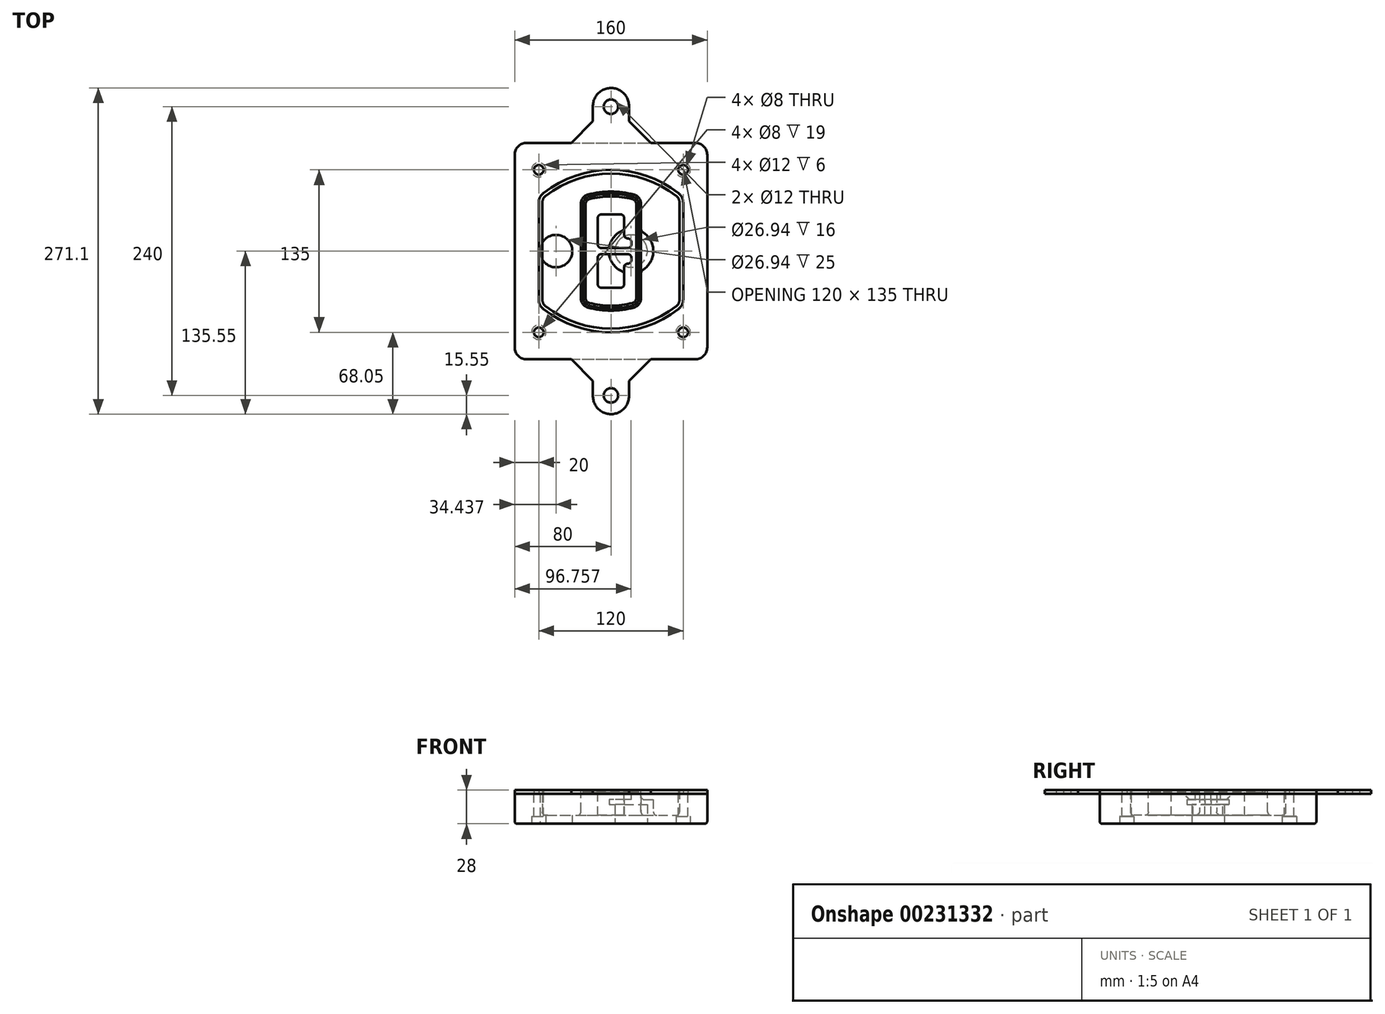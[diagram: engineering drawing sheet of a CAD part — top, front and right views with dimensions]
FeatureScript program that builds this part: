
annotation { "Feature Type Name" : "Feature", "Feature Type Description" : "" }
export const myFeature = defineFeature(function(context is Context, id is Id, definition is map)
    precondition{}
    {
        {
            var Q0;
            Q0=qCreatedBy(makeId("Top.planeOp"),FACE);
            var sketch = newSketch(context, id + "F0", { "sketchPlane" : qUnion([Q0])});
            skPoint(sketch, "E0.rect.middle", {"position": v(0, 0) * mm});
            skLineSegment(sketch, "E1.bottom", {"start": v(-70, -90) * mm, "end": v(70, -90) * mm});
            skLineSegment(sketch, "E1.top", {"start": v(-70, 90) * mm, "end": v(70, 90) * mm});
            skLineSegment(sketch, "E1.left", {"start": v(-80, -80) * mm, "end": v(-80, 80) * mm});
            skLineSegment(sketch, "E1.right", {"start": v(80, -80) * mm, "end": v(80, 80) * mm});
            skLineSegment(sketch, "E2", {"start": v(-80, 90) * mm, "end": v(80, -90) * mm, "construction": true});
            skLineSegment(sketch, "E3", {"start": v(80, 90) * mm, "end": v(-80, -90) * mm, "construction": true});
            skCircle(sketch, "E4", {"center": v(-60, 67.5) * mm, "radius": 4 * mm});
            skCircle(sketch, "E5", {"center": v(60, 67.5) * mm, "radius": 4 * mm});
            skCircle(sketch, "E6", {"center": v(60, -67.5) * mm, "radius": 4 * mm});
            skCircle(sketch, "E7", {"center": v(-60, -67.5) * mm, "radius": 4 * mm});
            skLineSegment(sketch, "E8", {"start": v(-60, 67.5) * mm, "end": v(60, 67.5) * mm, "construction": true});
            skLineSegment(sketch, "E9", {"start": v(60, 67.5) * mm, "end": v(60, -67.5) * mm, "construction": true});
            skLineSegment(sketch, "E10", {"start": v(60, -67.5) * mm, "end": v(-60, -67.5) * mm, "construction": true});
            skLineSegment(sketch, "E11", {"start": v(-60, -67.5) * mm, "end": v(-60, 67.5) * mm, "construction": true});
            skLineSegment(sketch, "E12", {"start": v(-60, 40.3) * mm, "end": v(-60, -40.3) * mm});
            skLineSegment(sketch, "E13", {"start": v(60, 40.3) * mm, "end": v(60, -40.3) * mm});
            skArc(sketch, "E14", {"start": v(56.15, 48.18) * mm, "mid": v(0, 67.5) * mm, "end": v(-56.15, 48.18) * mm});
            skArc(sketch, "E15", {"start": v(-56.15, -48.18) * mm, "mid": v(0, -67.5) * mm, "end": v(56.15, -48.18) * mm});
            skLineSegment(sketch, "E16", {"start": v(-60, 0) * mm, "end": v(60, 0) * mm, "construction": true});
            skPoint(sketch, "E17.visualSharp", {"position": v(-60, -45) * mm});
            skArc(sketch, "E17.filletArc", {"start": v(-60, -40.3) * mm, "mid": v(-58.99, -44.68) * mm, "end": v(-56.15, -48.18) * mm});
            skPoint(sketch, "E18.visualSharp", {"position": v(-60, 45) * mm});
            skArc(sketch, "E18.filletArc", {"start": v(-56.15, 48.18) * mm, "mid": v(-58.99, 44.68) * mm, "end": v(-60, 40.3) * mm});
            skPoint(sketch, "E19.visualSharp", {"position": v(60, 45) * mm});
            skArc(sketch, "E19.filletArc", {"start": v(60, 40.3) * mm, "mid": v(58.99, 44.68) * mm, "end": v(56.15, 48.18) * mm});
            skPoint(sketch, "E20.visualSharp", {"position": v(60, -45) * mm});
            skArc(sketch, "E20.filletArc", {"start": v(56.15, -48.18) * mm, "mid": v(58.99, -44.68) * mm, "end": v(60, -40.3) * mm});
            skPoint(sketch, "E21.visualSharp", {"position": v(-80, 90) * mm});
            skArc(sketch, "E21.filletArc", {"start": v(-70, 90) * mm, "mid": v(-77.07, 87.07) * mm, "end": v(-80, 80) * mm});
            skPoint(sketch, "E22.visualSharp", {"position": v(80, 90) * mm});
            skArc(sketch, "E22.filletArc", {"start": v(80, 80) * mm, "mid": v(77.07, 87.07) * mm, "end": v(70, 90) * mm});
            skPoint(sketch, "E23.visualSharp", {"position": v(80, -90) * mm});
            skArc(sketch, "E23.filletArc", {"start": v(70, -90) * mm, "mid": v(77.07, -87.07) * mm, "end": v(80, -80) * mm});
            skPoint(sketch, "E24.visualSharp", {"position": v(-80, -90) * mm});
            skArc(sketch, "E24.filletArc", {"start": v(-80, -80) * mm, "mid": v(-77.07, -87.07) * mm, "end": v(-70, -90) * mm});
            skArc(sketch, "E25.0", {"start": v(57, 40.3) * mm, "mid": v(56.3, 43.36) * mm, "end": v(54.3, 45.81) * mm});
            skLineSegment(sketch, "E25.1", {"start": v(57, 40.3) * mm, "end": v(57, -40.3) * mm});
            skArc(sketch, "E25.2", {"start": v(54.3, -45.81) * mm, "mid": v(56.3, -43.36) * mm, "end": v(57, -40.3) * mm});
            skArc(sketch, "E25.3", {"start": v(-54.3, -45.81) * mm, "mid": v(0, -64.5) * mm, "end": v(54.3, -45.81) * mm});
            skArc(sketch, "E25.4", {"start": v(-57, -40.3) * mm, "mid": v(-56.3, -43.36) * mm, "end": v(-54.3, -45.81) * mm});
            skArc(sketch, "E25.5", {"start": v(54.3, 45.81) * mm, "mid": v(0, 64.5) * mm, "end": v(-54.3, 45.81) * mm});
            skLineSegment(sketch, "E25.6", {"start": v(-57, 40.3) * mm, "end": v(-57, -40.3) * mm});
            skArc(sketch, "E25.7", {"start": v(-54.3, 45.81) * mm, "mid": v(-56.3, 43.36) * mm, "end": v(-57, 40.3) * mm});
            skArc(sketch, "E26.0", {"start": v(-58.62, 51.33) * mm, "mid": v(-62.58, 46.43) * mm, "end": v(-64, 40.3) * mm});
            skArc(sketch, "E26.1", {"start": v(58.62, 51.33) * mm, "mid": v(0, 71.5) * mm, "end": v(-58.62, 51.33) * mm});
            skArc(sketch, "E26.2", {"start": v(64, 40.3) * mm, "mid": v(62.58, 46.43) * mm, "end": v(58.62, 51.33) * mm});
            skLineSegment(sketch, "E26.3", {"start": v(64, 40.3) * mm, "end": v(64, -40.3) * mm});
            skArc(sketch, "E26.4", {"start": v(58.62, -51.33) * mm, "mid": v(62.58, -46.43) * mm, "end": v(64, -40.3) * mm});
            skLineSegment(sketch, "E26.5", {"start": v(-64, 40.3) * mm, "end": v(-64, -40.3) * mm});
            skArc(sketch, "E26.6", {"start": v(-58.62, -51.33) * mm, "mid": v(0, -71.5) * mm, "end": v(58.62, -51.33) * mm});
            skArc(sketch, "E26.7", {"start": v(-64, -40.3) * mm, "mid": v(-62.58, -46.43) * mm, "end": v(-58.62, -51.33) * mm});
            skSolve(sketch);
        }
        {
            var Q0;
            Q0=makeQuery(id+"F0.imprint","IMPRINT",FACE,{"disambiguationData":[TD([[makeQuery(id+"F0.imprint","IMPRINT",EDGE,{"derivedFrom":sQuery(id+"F0.wireOp",EDGE,"E1.bottom")}),1.0]])]});
            var Q1;
            Q1=makeQuery(id+"F0.imprint","IMPRINT",FACE,{"disambiguationData":[TD([[makeQuery(id+"F0.imprint","IMPRINT",EDGE,{"derivedFrom":sQuery(id+"F0.wireOp",EDGE,"E12")}),1.0]])]});
            var Q2;
            Q2=makeQuery(id+"F0.imprint","IMPRINT",FACE,{"disambiguationData":[TD([[makeQuery(id+"F0.imprint","IMPRINT",EDGE,{"derivedFrom":sQuery(id+"F0.wireOp",EDGE,"E25.0")}),1.0]])]});
            var Q3;
            Q3=makeQuery(id+"F0.imprint","IMPRINT",FACE,{"disambiguationData":[TD([[makeQuery(id+"F0.imprint","IMPRINT",EDGE,{"derivedFrom":sQuery(id+"F0.wireOp",EDGE,"E12")}),-1.0]])]});
            extrude(context, id + "F1", {"entities" : qUnion([Q0, Q1, Q2, Q3]), "oppositeDirection" : true, "depth" : 25 * mm});
        }
        {
            var Q0;
            Q0=makeQuery(id+"F0.imprint","IMPRINT",FACE,{"disambiguationData":[TD([[makeQuery(id+"F0.imprint","IMPRINT",EDGE,{"derivedFrom":sQuery(id+"F0.wireOp",EDGE,"E12")}),1.0]])]});
            extrude(context, id + "F2", {"entities" : qUnion([Q0]), "operationType" : NewBodyOperationType.ADD, "depth" : 3 * mm});
        }
        {
            var Q0;
            Q0=makeQuery(id+"F0.imprint","IMPRINT",FACE,{"disambiguationData":[TD([[makeQuery(id+"F0.imprint","IMPRINT",EDGE,{"derivedFrom":sQuery(id+"F0.wireOp",EDGE,"E25.0")}),1.0]])]});
            extrude(context, id + "F3", {"entities" : qUnion([Q0]), "operationType" : NewBodyOperationType.REMOVE, "oppositeDirection" : true, "depth" : 18 * mm});
        }
        {
            var Q0;
            Q0=makeQuery(id+"F2.opExtrude","CAP_FACE",FACE,{"disambiguationData":[OSD([sQuery(id+"F0.wireOp",EDGE,"E12"),sQuery(id+"F0.wireOp",EDGE,"E13"),sQuery(id+"F0.wireOp",EDGE,"E14"),sQuery(id+"F0.wireOp",EDGE,"E15"),sQuery(id+"F0.wireOp",EDGE,"E17.filletArc"),sQuery(id+"F0.wireOp",EDGE,"E18.filletArc"),sQuery(id+"F0.wireOp",EDGE,"E19.filletArc"),sQuery(id+"F0.wireOp",EDGE,"E20.filletArc"),sQuery(id+"F0.wireOp",EDGE,"E25.0"),sQuery(id+"F0.wireOp",EDGE,"E25.1"),sQuery(id+"F0.wireOp",EDGE,"E25.2"),sQuery(id+"F0.wireOp",EDGE,"E25.3"),sQuery(id+"F0.wireOp",EDGE,"E25.4"),sQuery(id+"F0.wireOp",EDGE,"E25.5"),sQuery(id+"F0.wireOp",EDGE,"E25.6"),sQuery(id+"F0.wireOp",EDGE,"E25.7")])],"isStart":false});
            var sketch = newSketch(context, id + "F4", { "sketchPlane" : qUnion([Q0])});
            skArc(sketch, "E27.0", {"start": v(-19.08, -46.97) * mm, "mid": v(0, -49.5) * mm, "end": v(19.08, -46.97) * mm});
            skArc(sketch, "E28.0", {"start": v(19.08, 46.97) * mm, "mid": v(0, 49.5) * mm, "end": v(-19.08, 46.97) * mm});
            skLineSegment(sketch, "E29", {"start": v(-25, 39.25) * mm, "end": v(-25, -39.25) * mm});
            skLineSegment(sketch, "E30", {"start": v(25, 39.25) * mm, "end": v(25, -39.25) * mm});
            skLineSegment(sketch, "E31", {"start": v(-25, 45.1) * mm, "end": v(25, 45.1) * mm, "construction": true});
            skLineSegment(sketch, "E32", {"start": v(-25, -45.1) * mm, "end": v(25, -45.1) * mm, "construction": true});
            skPoint(sketch, "E33.visualSharp", {"position": v(-25, 45.1) * mm});
            skArc(sketch, "E33.filletArc", {"start": v(-19.08, 46.97) * mm, "mid": v(-23.35, 44.11) * mm, "end": v(-25, 39.25) * mm});
            skPoint(sketch, "E34.visualSharp", {"position": v(25, 45.1) * mm});
            skArc(sketch, "E34.filletArc", {"start": v(25, 39.25) * mm, "mid": v(23.35, 44.11) * mm, "end": v(19.08, 46.97) * mm});
            skPoint(sketch, "E35.visualSharp", {"position": v(25, -45.1) * mm});
            skArc(sketch, "E35.filletArc", {"start": v(19.08, -46.97) * mm, "mid": v(23.35, -44.11) * mm, "end": v(25, -39.25) * mm});
            skPoint(sketch, "E36.visualSharp", {"position": v(-25, -45.1) * mm});
            skArc(sketch, "E36.filletArc", {"start": v(-25, -39.25) * mm, "mid": v(-23.35, -44.11) * mm, "end": v(-19.08, -46.97) * mm});
            skArc(sketch, "E37.0", {"start": v(54.3, 45.81) * mm, "mid": v(0, 64.5) * mm, "end": v(-54.3, 45.81) * mm});
            skArc(sketch, "E37.1", {"start": v(-54.3, 45.81) * mm, "mid": v(-56.3, 43.36) * mm, "end": v(-57, 40.3) * mm});
            skLineSegment(sketch, "E37.2", {"start": v(-57, 40.3) * mm, "end": v(-57, -40.3) * mm});
            skArc(sketch, "E37.3", {"start": v(-57, -40.3) * mm, "mid": v(-56.3, -43.36) * mm, "end": v(-54.3, -45.81) * mm});
            skArc(sketch, "E37.4", {"start": v(-54.3, -45.81) * mm, "mid": v(0, -64.5) * mm, "end": v(54.3, -45.81) * mm});
            skArc(sketch, "E37.5", {"start": v(54.3, -45.81) * mm, "mid": v(56.3, -43.36) * mm, "end": v(57, -40.3) * mm});
            skLineSegment(sketch, "E37.6", {"start": v(57, 40.3) * mm, "end": v(57, -40.3) * mm});
            skArc(sketch, "E37.7", {"start": v(57, 40.3) * mm, "mid": v(56.3, 43.36) * mm, "end": v(54.3, 45.81) * mm});
            skLineSegment(sketch, "E38.0", {"start": v(23, 39.25) * mm, "end": v(23, -39.25) * mm});
            skArc(sketch, "E38.1", {"start": v(18.56, -45.04) * mm, "mid": v(21.76, -42.9) * mm, "end": v(23, -39.25) * mm});
            skArc(sketch, "E38.2", {"start": v(-18.56, -45.04) * mm, "mid": v(0, -47.5) * mm, "end": v(18.56, -45.04) * mm});
            skArc(sketch, "E38.3", {"start": v(-23, -39.25) * mm, "mid": v(-21.76, -42.9) * mm, "end": v(-18.56, -45.04) * mm});
            skLineSegment(sketch, "E38.4", {"start": v(-23, 39.25) * mm, "end": v(-23, -39.25) * mm});
            skArc(sketch, "E38.5", {"start": v(23, 39.25) * mm, "mid": v(21.76, 42.9) * mm, "end": v(18.56, 45.04) * mm});
            skArc(sketch, "E38.6", {"start": v(-18.56, 45.04) * mm, "mid": v(-21.76, 42.9) * mm, "end": v(-23, 39.25) * mm});
            skArc(sketch, "E38.7", {"start": v(18.56, 45.04) * mm, "mid": v(0, 47.5) * mm, "end": v(-18.56, 45.04) * mm});
            skArc(sketch, "E39.0", {"start": v(21, 39.25) * mm, "mid": v(20.18, 41.68) * mm, "end": v(18.04, 43.1) * mm});
            skLineSegment(sketch, "E39.1", {"start": v(21, 39.25) * mm, "end": v(21, -39.25) * mm});
            skArc(sketch, "E39.2", {"start": v(18.04, -43.1) * mm, "mid": v(20.18, -41.68) * mm, "end": v(21, -39.25) * mm});
            skArc(sketch, "E39.3", {"start": v(-18.04, -43.1) * mm, "mid": v(0, -45.5) * mm, "end": v(18.04, -43.1) * mm});
            skArc(sketch, "E39.4", {"start": v(-21, -39.25) * mm, "mid": v(-20.18, -41.68) * mm, "end": v(-18.04, -43.1) * mm});
            skArc(sketch, "E39.5", {"start": v(18.04, 43.1) * mm, "mid": v(0, 45.5) * mm, "end": v(-18.04, 43.1) * mm});
            skLineSegment(sketch, "E39.6", {"start": v(-21, 39.25) * mm, "end": v(-21, -39.25) * mm});
            skArc(sketch, "E39.7", {"start": v(-18.04, 43.1) * mm, "mid": v(-20.18, 41.68) * mm, "end": v(-21, 39.25) * mm});
            skLineSegment(sketch, "E40", {"start": v(-25, 0) * mm, "end": v(25, 0) * mm, "construction": true});
            skLineSegment(sketch, "E41", {"start": v(-11, 5.5) * mm, "end": v(-11, 27.5) * mm});
            skLineSegment(sketch, "E42", {"start": v(-8, 30.5) * mm, "end": v(8, 30.5) * mm});
            skLineSegment(sketch, "E43", {"start": v(11, 27.5) * mm, "end": v(11, 13.5) * mm});
            skLineSegment(sketch, "E44", {"start": v(14, 10.5) * mm, "end": v(14, 10.5) * mm});
            skLineSegment(sketch, "E45", {"start": v(17, 7.5) * mm, "end": v(17, 5.5) * mm});
            skLineSegment(sketch, "E46", {"start": v(14, 2.5) * mm, "end": v(-8, 2.5) * mm});
            skPoint(sketch, "E47.visualSharp", {"position": v(-11, 30.5) * mm});
            skArc(sketch, "E47.filletArc", {"start": v(-8, 30.5) * mm, "mid": v(-10.12, 29.62) * mm, "end": v(-11, 27.5) * mm});
            skPoint(sketch, "E48.visualSharp", {"position": v(11, 30.5) * mm});
            skArc(sketch, "E48.filletArc", {"start": v(11, 27.5) * mm, "mid": v(10.12, 29.62) * mm, "end": v(8, 30.5) * mm});
            skPoint(sketch, "E49.visualSharp", {"position": v(11, 10.5) * mm});
            skArc(sketch, "E49.filletArc", {"start": v(11, 13.5) * mm, "mid": v(11.88, 11.38) * mm, "end": v(14, 10.5) * mm});
            skPoint(sketch, "E50.visualSharp", {"position": v(17, 10.5) * mm});
            skArc(sketch, "E50.filletArc", {"start": v(17, 7.5) * mm, "mid": v(16.12, 9.62) * mm, "end": v(14, 10.5) * mm});
            skPoint(sketch, "E51.visualSharp", {"position": v(17, 2.5) * mm});
            skArc(sketch, "E51.filletArc", {"start": v(14, 2.5) * mm, "mid": v(16.12, 3.38) * mm, "end": v(17, 5.5) * mm});
            skPoint(sketch, "E52.visualSharp", {"position": v(-11, 2.5) * mm});
            skArc(sketch, "E52.filletArc", {"start": v(-11, 5.5) * mm, "mid": v(-10.12, 3.38) * mm, "end": v(-8, 2.5) * mm});
            skLineSegment(sketch, "E53.0.MirrorCS", {"start": v(14, -2.5) * mm, "end": v(-8, -2.5) * mm});
            skArc(sketch, "E54.0.MirrorCS", {"start": v(-11, -5.5) * mm, "mid": v(-10.12, -3.38) * mm, "end": v(-8, -2.5) * mm});
            skLineSegment(sketch, "E55.0.MirrorCS", {"start": v(-11, -5.5) * mm, "end": v(-11, -27.5) * mm});
            skArc(sketch, "E56.0.MirrorCS", {"start": v(-8, -30.5) * mm, "mid": v(-10.12, -29.62) * mm, "end": v(-11, -27.5) * mm});
            skLineSegment(sketch, "E57.0.MirrorCS", {"start": v(-8, -30.5) * mm, "end": v(8, -30.5) * mm});
            skArc(sketch, "E58.0.MirrorCS", {"start": v(11, -27.5) * mm, "mid": v(10.12, -29.62) * mm, "end": v(8, -30.5) * mm});
            skLineSegment(sketch, "E59.0.MirrorCS", {"start": v(11, -27.5) * mm, "end": v(11, -13.5) * mm});
            skArc(sketch, "E60.0.MirrorCS", {"start": v(11, -13.5) * mm, "mid": v(11.88, -11.38) * mm, "end": v(14, -10.5) * mm});
            skArc(sketch, "E61.0.MirrorCS", {"start": v(17, -7.5) * mm, "mid": v(16.12, -9.62) * mm, "end": v(14, -10.5) * mm});
            skLineSegment(sketch, "E62.0.MirrorCS", {"start": v(17, -7.5) * mm, "end": v(17, -5.5) * mm});
            skArc(sketch, "E63.0.MirrorCS", {"start": v(14, -2.5) * mm, "mid": v(16.12, -3.38) * mm, "end": v(17, -5.5) * mm});
            skSolve(sketch);
        }
        {
            var Q0;
            Q0=makeQuery(id+"F4.imprint","IMPRINT",FACE,{"disambiguationData":[TD([[makeQuery(id+"F4.imprint","IMPRINT",EDGE,{"derivedFrom":sQuery(id+"F4.wireOp",EDGE,"E27.0")}),1.0]])]});
            var Q1;
            Q1=makeQuery(id+"F4.imprint","IMPRINT",FACE,{"disambiguationData":[TD([[makeQuery(id+"F4.imprint","IMPRINT",EDGE,{"derivedFrom":sQuery(id+"F4.wireOp",EDGE,"E38.0")}),-1.0]])]});
            var Q2;
            Q2=makeQuery(id+"F4.imprint","IMPRINT",FACE,{"disambiguationData":[TD([[makeQuery(id+"F4.imprint","IMPRINT",EDGE,{"derivedFrom":sQuery(id+"F4.wireOp",EDGE,"E39.0")}),1.0]])]});
            extrude(context, id + "F5", {"entities" : qUnion([Q0, Q1, Q2]), "operationType" : NewBodyOperationType.ADD, "endBound" : BoundingType.UP_TO_NEXT, "oppositeDirection" : true, "depth" : 25 * mm});
        }
        {
            var Q0;
            Q0=makeQuery(id+"F4.imprint","IMPRINT",FACE,{"disambiguationData":[TD([[makeQuery(id+"F4.imprint","IMPRINT",EDGE,{"derivedFrom":sQuery(id+"F4.wireOp",EDGE,"E38.0")}),-1.0]])]});
            extrude(context, id + "F6", {"entities" : qUnion([Q0]), "operationType" : NewBodyOperationType.REMOVE, "oppositeDirection" : true, "depth" : 2 * mm});
        }
        {
            var Q0;
            Q0=makeQuery(id+"F1.opExtrude","CAP_FACE",FACE,{"disambiguationData":[OSD([sQuery(id+"F0.wireOp",EDGE,"E1.bottom"),sQuery(id+"F0.wireOp",EDGE,"E1.top"),sQuery(id+"F0.wireOp",EDGE,"E1.left"),sQuery(id+"F0.wireOp",EDGE,"E1.right"),sQuery(id+"F0.wireOp",EDGE,"E4"),sQuery(id+"F0.wireOp",EDGE,"E5"),sQuery(id+"F0.wireOp",EDGE,"E6"),sQuery(id+"F0.wireOp",EDGE,"E7"),sQuery(id+"F0.wireOp",EDGE,"E21.filletArc"),sQuery(id+"F0.wireOp",EDGE,"E22.filletArc"),sQuery(id+"F0.wireOp",EDGE,"E23.filletArc"),sQuery(id+"F0.wireOp",EDGE,"E24.filletArc")])],"isStart":false});
            var sketch = newSketch(context, id + "F7", { "sketchPlane" : qUnion([Q0])});
            skCircle(sketch, "E64", {"center": v(16.76, 0) * mm, "radius": 13.47 * mm});
            skCircle(sketch, "E65", {"center": v(-45.56, 0) * mm, "radius": 13.47 * mm});
            skLineSegment(sketch, "E66", {"start": v(80, 0) * mm, "end": v(-80, 0) * mm});
            skCircle(sketch, "E67", {"center": v(16.76, 0) * mm, "radius": 18.47 * mm});
            skCircle(sketch, "E68", {"center": v(60, -67.5) * mm, "radius": 6 * mm});
            skCircle(sketch, "E69", {"center": v(-60, -67.5) * mm, "radius": 6 * mm});
            skCircle(sketch, "E70", {"center": v(-60, 67.5) * mm, "radius": 6 * mm});
            skCircle(sketch, "E71", {"center": v(60, 67.5) * mm, "radius": 6 * mm});
            skSolve(sketch);
        }
        {
            var Q0;
            {var subQ1=sQuery(id+"F7.wireOp",EDGE,"E66");var subQ4=sQuery(id+"F7.wireOp",EDGE,"E64");var subQ6=makeQuery(id+"F7.imprint","INTERSECT",VERTEX,{"disambiguationData":[OD(0.0)],"derivedFrom":[subQ4,subQ1]});Q0=makeQuery(id+"F7.imprint","IMPRINT",FACE,{"disambiguationData":[TD([[makeQuery(id+"F7.imprint","IMPRINT",EDGE,{"disambiguationData":[TD([[subQ6,-1.0]])],"derivedFrom":subQ4}),-1.0]])]});}
            var Q1;
            {var subQ0=sQuery(id+"F7.wireOp",EDGE,"E66");var subQ1=sQuery(id+"F7.wireOp",EDGE,"E64");var subQ3=makeQuery(id+"F7.imprint","INTERSECT",VERTEX,{"disambiguationData":[OD(0.0)],"derivedFrom":[subQ1,subQ0]});Q1=makeQuery(id+"F7.imprint","IMPRINT",FACE,{"disambiguationData":[TD([[makeQuery(id+"F7.imprint","IMPRINT",EDGE,{"disambiguationData":[TD([[subQ3,-1.0]])],"derivedFrom":subQ1}),1.0]])]});}
            var Q2;
            {var subQ0=sQuery(id+"F7.wireOp",EDGE,"E66");var subQ1=sQuery(id+"F7.wireOp",EDGE,"E64");var subQ3=makeQuery(id+"F7.imprint","INTERSECT",VERTEX,{"disambiguationData":[OD(0.0)],"derivedFrom":[subQ1,subQ0]});Q2=makeQuery(id+"F7.imprint","IMPRINT",FACE,{"disambiguationData":[TD([[makeQuery(id+"F7.imprint","IMPRINT",EDGE,{"disambiguationData":[TD([[subQ3,1.0]])],"derivedFrom":subQ1}),1.0]])]});}
            var Q3;
            {var subQ1=sQuery(id+"F7.wireOp",EDGE,"E66");var subQ4=sQuery(id+"F7.wireOp",EDGE,"E64");var subQ6=makeQuery(id+"F7.imprint","INTERSECT",VERTEX,{"disambiguationData":[OD(0.0)],"derivedFrom":[subQ4,subQ1]});Q3=makeQuery(id+"F7.imprint","IMPRINT",FACE,{"disambiguationData":[TD([[makeQuery(id+"F7.imprint","IMPRINT",EDGE,{"disambiguationData":[TD([[subQ6,1.0]])],"derivedFrom":subQ4}),-1.0]])]});}
            extrude(context, id + "F8", {"entities" : qUnion([Q0, Q1, Q2, Q3]), "operationType" : NewBodyOperationType.ADD, "oppositeDirection" : true, "depth" : 20 * mm});
        }
        {
            var Q0;
            {var subQ0=sQuery(id+"F7.wireOp",EDGE,"E66");var subQ1=sQuery(id+"F7.wireOp",EDGE,"E64");var subQ3=makeQuery(id+"F7.imprint","INTERSECT",VERTEX,{"disambiguationData":[OD(0.0)],"derivedFrom":[subQ1,subQ0]});Q0=makeQuery(id+"F7.imprint","IMPRINT",FACE,{"disambiguationData":[TD([[makeQuery(id+"F7.imprint","IMPRINT",EDGE,{"disambiguationData":[TD([[subQ3,-1.0]])],"derivedFrom":subQ1}),1.0]])]});}
            var Q1;
            {var subQ0=sQuery(id+"F7.wireOp",EDGE,"E66");var subQ1=sQuery(id+"F7.wireOp",EDGE,"E64");var subQ3=makeQuery(id+"F7.imprint","INTERSECT",VERTEX,{"disambiguationData":[OD(0.0)],"derivedFrom":[subQ1,subQ0]});Q1=makeQuery(id+"F7.imprint","IMPRINT",FACE,{"disambiguationData":[TD([[makeQuery(id+"F7.imprint","IMPRINT",EDGE,{"disambiguationData":[TD([[subQ3,1.0]])],"derivedFrom":subQ1}),1.0]])]});}
            extrude(context, id + "F9", {"entities" : qUnion([Q0, Q1]), "operationType" : NewBodyOperationType.REMOVE, "oppositeDirection" : true, "depth" : 16 * mm});
        }
        {
            var Q0;
            {var subQ0=sQuery(id+"F7.wireOp",EDGE,"E66");var subQ1=sQuery(id+"F7.wireOp",EDGE,"E65");var subQ3=makeQuery(id+"F7.imprint","INTERSECT",VERTEX,{"disambiguationData":[OD(0.0)],"derivedFrom":[subQ1,subQ0]});Q0=makeQuery(id+"F7.imprint","IMPRINT",FACE,{"disambiguationData":[TD([[makeQuery(id+"F7.imprint","IMPRINT",EDGE,{"disambiguationData":[TD([[subQ3,-1.0]])],"derivedFrom":subQ1}),1.0]])]});}
            var Q1;
            {var subQ0=sQuery(id+"F7.wireOp",EDGE,"E66");var subQ1=sQuery(id+"F7.wireOp",EDGE,"E65");var subQ3=makeQuery(id+"F7.imprint","INTERSECT",VERTEX,{"disambiguationData":[OD(0.0)],"derivedFrom":[subQ1,subQ0]});Q1=makeQuery(id+"F7.imprint","IMPRINT",FACE,{"disambiguationData":[TD([[makeQuery(id+"F7.imprint","IMPRINT",EDGE,{"disambiguationData":[TD([[subQ3,1.0]])],"derivedFrom":subQ1}),1.0]])]});}
            extrude(context, id + "F10", {"entities" : qUnion([Q0, Q1]), "operationType" : NewBodyOperationType.REMOVE, "oppositeDirection" : true, "depth" : 25 * mm});
        }
        {
            var Q0;
            Q0=makeQuery(id+"F7.imprint","IMPRINT",FACE,{"disambiguationData":[TD([[makeQuery(id+"F7.imprint","IMPRINT",EDGE,{"derivedFrom":sQuery(id+"F7.wireOp",EDGE,"E68")}),1.0]])]});
            var Q1;
            Q1=makeQuery(id+"F7.imprint","IMPRINT",FACE,{"disambiguationData":[TD([[makeQuery(id+"F7.imprint","IMPRINT",EDGE,{"derivedFrom":makeQuery(id+"F1.opExtrude","CAP_EDGE",EDGE,{"disambiguationData":[OSD([sQuery(id+"F0.wireOp",EDGE,"E5")])],"isStart":false})}),-1.0]])]});
            var Q2;
            Q2=makeQuery(id+"F7.imprint","IMPRINT",FACE,{"disambiguationData":[TD([[makeQuery(id+"F7.imprint","IMPRINT",EDGE,{"derivedFrom":sQuery(id+"F7.wireOp",EDGE,"E69")}),1.0]])]});
            var Q3;
            Q3=makeQuery(id+"F7.imprint","IMPRINT",FACE,{"disambiguationData":[TD([[makeQuery(id+"F7.imprint","IMPRINT",EDGE,{"derivedFrom":makeQuery(id+"F1.opExtrude","CAP_EDGE",EDGE,{"disambiguationData":[OSD([sQuery(id+"F0.wireOp",EDGE,"E4")])],"isStart":false})}),-1.0]])]});
            var Q4;
            Q4=makeQuery(id+"F7.imprint","IMPRINT",FACE,{"disambiguationData":[TD([[makeQuery(id+"F7.imprint","IMPRINT",EDGE,{"derivedFrom":sQuery(id+"F7.wireOp",EDGE,"E70")}),1.0]])]});
            var Q5;
            Q5=makeQuery(id+"F7.imprint","IMPRINT",FACE,{"disambiguationData":[TD([[makeQuery(id+"F7.imprint","IMPRINT",EDGE,{"derivedFrom":makeQuery(id+"F1.opExtrude","CAP_EDGE",EDGE,{"disambiguationData":[OSD([sQuery(id+"F0.wireOp",EDGE,"E7")])],"isStart":false})}),-1.0]])]});
            var Q6;
            Q6=makeQuery(id+"F7.imprint","IMPRINT",FACE,{"disambiguationData":[TD([[makeQuery(id+"F7.imprint","IMPRINT",EDGE,{"derivedFrom":sQuery(id+"F7.wireOp",EDGE,"E71")}),1.0]])]});
            var Q7;
            Q7=makeQuery(id+"F7.imprint","IMPRINT",FACE,{"disambiguationData":[TD([[makeQuery(id+"F7.imprint","IMPRINT",EDGE,{"derivedFrom":makeQuery(id+"F1.opExtrude","CAP_EDGE",EDGE,{"disambiguationData":[OSD([sQuery(id+"F0.wireOp",EDGE,"E6")])],"isStart":false})}),-1.0]])]});
            extrude(context, id + "F11", {"entities" : qUnion([Q0, Q1, Q2, Q3, Q4, Q5, Q6, Q7]), "operationType" : NewBodyOperationType.REMOVE, "oppositeDirection" : true, "depth" : 6 * mm});
        }
        {
            var Q0;
            Q0=makeQuery(id+"F9.boolean.opBoolean","COPY",FACE,{"derivedFrom":makeQuery(id+"F9.opExtrude","CAP_FACE",FACE,{"disambiguationData":[OSD([sQuery(id+"F7.wireOp",EDGE,"E64")])],"isStart":false})});
            var sketch = newSketch(context, id + "F12", { "sketchPlane" : qUnion([Q0])});
            skArc(sketch, "E72.0", {"start": v(11, 17.55) * mm, "mid": v(2.57, 11.82) * mm, "end": v(-1.54, 2.5) * mm});
            skArc(sketch, "E72.1", {"start": v(-1.54, -2.5) * mm, "mid": v(2.57, -11.82) * mm, "end": v(11, -17.55) * mm});
            skLineSegment(sketch, "E73", {"start": v(-1.54, -2.5) * mm, "end": v(14, -2.5) * mm});
            skLineSegment(sketch, "E74.0", {"start": v(14, 2.5) * mm, "end": v(-1.54, 2.5) * mm});
            skArc(sketch, "E74.1", {"start": v(14, 2.5) * mm, "mid": v(16.12, 3.38) * mm, "end": v(17, 5.5) * mm});
            skLineSegment(sketch, "E74.2", {"start": v(17, 7.5) * mm, "end": v(17, 5.5) * mm});
            skArc(sketch, "E74.3", {"start": v(17, 7.5) * mm, "mid": v(16.12, 9.62) * mm, "end": v(14, 10.5) * mm});
            skArc(sketch, "E74.4", {"start": v(11, 13.5) * mm, "mid": v(11.88, 11.38) * mm, "end": v(14, 10.5) * mm});
            skLineSegment(sketch, "E74.5", {"start": v(11, 17.55) * mm, "end": v(11, 13.5) * mm});
            skLineSegment(sketch, "E74.7", {"start": v(14, -2.5) * mm, "end": v(-1.54, -2.5) * mm});
            skArc(sketch, "E74.8", {"start": v(14, -2.5) * mm, "mid": v(16.12, -3.38) * mm, "end": v(17, -5.5) * mm});
            skLineSegment(sketch, "E74.9", {"start": v(17, -7.5) * mm, "end": v(17, -5.5) * mm});
            skArc(sketch, "E74.10", {"start": v(17, -7.5) * mm, "mid": v(16.12, -9.62) * mm, "end": v(14, -10.5) * mm});
            skArc(sketch, "E74.11", {"start": v(11, -13.5) * mm, "mid": v(11.88, -11.38) * mm, "end": v(14, -10.5) * mm});
            skLineSegment(sketch, "E74.12", {"start": v(11, -17.55) * mm, "end": v(11, -13.5) * mm});
            skPoint(sketch, "E75.orphan", {"position": v(11, -27.5) * mm});
            skPoint(sketch, "E76.orphan", {"position": v(-8, -2.5) * mm});
            skPoint(sketch, "E77.orphan", {"position": v(-8, 2.5) * mm});
            skPoint(sketch, "E78.orphan", {"position": v(11, 27.5) * mm});
            skSolve(sketch);
        }
        {
            var Q0;
            {var subQ7=sQuery(id+"F12.wireOp",EDGE,"E72.0");var subQ14=sQuery(id+"F12.wireOp",EDGE,"E72.1");var subQ16=sQuery(id+"F12.wireOp",EDGE,"E74.1");var subQ18=sQuery(id+"F12.wireOp",EDGE,"E74.8");Q0=qUnion([makeQuery(id+"F12.imprint","IMPRINT",FACE,{"disambiguationData":[TD([[makeQuery(id+"F12.imprint","IMPRINT",EDGE,{"derivedFrom":subQ7}),1.0]])]}),makeQuery(id+"F12.imprint","IMPRINT",FACE,{"disambiguationData":[TD([[makeQuery(id+"F12.imprint","IMPRINT",EDGE,{"derivedFrom":subQ14}),1.0]])]}),makeQuery(id+"F12.imprint","IMPRINT",FACE,{"disambiguationData":[TD([[makeQuery(id+"F12.imprint","IMPRINT",EDGE,{"derivedFrom":subQ16}),1.0]])]}),makeQuery(id+"F12.imprint","IMPRINT",FACE,{"disambiguationData":[TD([[makeQuery(id+"F12.imprint","IMPRINT",EDGE,{"derivedFrom":subQ18}),-1.0]])]})]);}
            var Q1;
            Q1=makeQuery(id+"F5.boolean.opBoolean","SPLIT",FACE,{"disambiguationData":[TD([makeQuery(id+"F5.opExtrude","SWEPT_FACE",FACE,{"disambiguationData":[OSD([sQuery(id+"F4.wireOp",EDGE,"E41")])]})])],"derivedFrom":makeQuery(id+"F3.boolean.opBoolean","COPY",FACE,{"derivedFrom":makeQuery(id+"F3.opExtrude","CAP_FACE",FACE,{"disambiguationData":[OSD([sQuery(id+"F0.wireOp",EDGE,"E25.0"),sQuery(id+"F0.wireOp",EDGE,"E25.1"),sQuery(id+"F0.wireOp",EDGE,"E25.2"),sQuery(id+"F0.wireOp",EDGE,"E25.3"),sQuery(id+"F0.wireOp",EDGE,"E25.4"),sQuery(id+"F0.wireOp",EDGE,"E25.5"),sQuery(id+"F0.wireOp",EDGE,"E25.6"),sQuery(id+"F0.wireOp",EDGE,"E25.7")])],"isStart":false})})});
            extrude(context, id + "F13", {"entities" : qUnion([Q0]), "operationType" : NewBodyOperationType.REMOVE, "endBound" : BoundingType.UP_TO_SURFACE, "endBoundEntityFace" : qUnion([Q1]), "depth" : 25 * mm});
        }
        {
            var Q0;
            Q0=makeQuery(id+"F3.boolean.opBoolean","COPY",EDGE,{"derivedFrom":makeQuery(id+"F3.opExtrude","CAP_EDGE",EDGE,{"disambiguationData":[OSD([sQuery(id+"F0.wireOp",EDGE,"E25.6")])],"isStart":false})});
            var Q1;
            Q1=makeQuery(id+"F8.boolean.opBoolean","INTERSECT",EDGE,{"derivedFrom":[makeQuery(id+"F5.opExtrude","SWEPT_FACE",FACE,{"disambiguationData":[OSD([sQuery(id+"F4.wireOp",EDGE,"E30")])]}),makeQuery(id+"F8.opExtrude","CAP_FACE",FACE,{"disambiguationData":[OSD([sQuery(id+"F7.wireOp",EDGE,"E67")])],"isStart":false})]});
            var Q2;
            Q2=makeQuery(id+"F8.boolean.opBoolean","INTERSECT",EDGE,{"disambiguationData":[OD(1.0)],"derivedFrom":[makeQuery(id+"F5.opExtrude","SWEPT_FACE",FACE,{"disambiguationData":[OSD([sQuery(id+"F4.wireOp",EDGE,"E30")])]}),makeQuery(id+"F8.opExtrude","SWEPT_FACE",FACE,{"disambiguationData":[OSD([sQuery(id+"F7.wireOp",EDGE,"E67")])]})]});
            var Q3;
            {var subQ0=sQuery(id+"F4.wireOp",EDGE,"E30");Q3=makeQuery(id+"F8.boolean.opBoolean","SPLIT",EDGE,{"disambiguationData":[TD([makeQuery(id+"F5.opExtrude","SWEPT_FACE",FACE,{"disambiguationData":[OSD([sQuery(id+"F4.wireOp",EDGE,"E35.filletArc")])]})])],"derivedFrom":makeQuery(id+"F5.opExtrude","CAP_EDGE",EDGE,{"disambiguationData":[OSD([subQ0])],"isStart":false})});}
            var Q4;
            {var subQ0=sQuery(id+"F0.wireOp",EDGE,"E25.7");var subQ1=sQuery(id+"F0.wireOp",EDGE,"E25.1");var subQ2=sQuery(id+"F0.wireOp",EDGE,"E25.6");var subQ3=sQuery(id+"F0.wireOp",EDGE,"E25.5");var subQ4=sQuery(id+"F0.wireOp",EDGE,"E25.4");var subQ5=sQuery(id+"F0.wireOp",EDGE,"E25.0");var subQ6=sQuery(id+"F0.wireOp",EDGE,"E25.2");var subQ7=sQuery(id+"F0.wireOp",EDGE,"E25.3");Q4=makeQuery(id+"F8.boolean.opBoolean","INTERSECT",EDGE,{"derivedFrom":[makeQuery(id+"F5.boolean.opBoolean","SPLIT",FACE,{"disambiguationData":[TD([makeQuery(id+"F2.opExtrude","SWEPT_FACE",FACE,{"disambiguationData":[OSD([subQ5])]})])],"derivedFrom":makeQuery(id+"F3.boolean.opBoolean","COPY",FACE,{"derivedFrom":makeQuery(id+"F3.opExtrude","CAP_FACE",FACE,{"disambiguationData":[OSD([subQ5,subQ1,subQ6,subQ7,subQ4,subQ3,subQ2,subQ0])],"isStart":false})})}),makeQuery(id+"F8.opExtrude","SWEPT_FACE",FACE,{"disambiguationData":[OSD([sQuery(id+"F7.wireOp",EDGE,"E67")])]})]});}
            var Q5;
            Q5=makeQuery(id+"F8.boolean.opBoolean","INTERSECT",EDGE,{"disambiguationData":[OD(0.0)],"derivedFrom":[makeQuery(id+"F5.opExtrude","SWEPT_FACE",FACE,{"disambiguationData":[OSD([sQuery(id+"F4.wireOp",EDGE,"E30")])]}),makeQuery(id+"F8.opExtrude","SWEPT_FACE",FACE,{"disambiguationData":[OSD([sQuery(id+"F7.wireOp",EDGE,"E67")])]})]});
            fillet(context, id + "F14", {"entities" : qUnion([Q0, Q1, Q2, Q3, Q4, Q5]), "radius" : 3 * mm, "tangentPropagation" : true, "allowEdgeOverflow" : false});
        }
        {
            var Q0;
            Q0=makeQuery(id+"F1.opExtrude","CAP_EDGE",EDGE,{"disambiguationData":[OSD([sQuery(id+"F0.wireOp",EDGE,"E1.bottom")])],"isStart":false});
            fillet(context, id + "F15", {"entities" : qUnion([Q0]), "radius" : 2 * mm, "tangentPropagation" : true, "allowEdgeOverflow" : false});
        }
        {
            var Q0;
            {var subQ0=sQuery(id+"F0.wireOp",EDGE,"E22.filletArc");var subQ1=sQuery(id+"F0.wireOp",EDGE,"E7");var subQ2=sQuery(id+"F0.wireOp",EDGE,"E6");var subQ3=sQuery(id+"F0.wireOp",EDGE,"E5");var subQ4=sQuery(id+"F0.wireOp",EDGE,"E4");var subQ5=sQuery(id+"F0.wireOp",EDGE,"E1.bottom");var subQ6=sQuery(id+"F0.wireOp",EDGE,"E21.filletArc");var subQ7=sQuery(id+"F0.wireOp",EDGE,"E1.top");var subQ8=sQuery(id+"F0.wireOp",EDGE,"E1.left");var subQ9=sQuery(id+"F0.wireOp",EDGE,"E1.right");var subQ10=sQuery(id+"F0.wireOp",EDGE,"E23.filletArc");var subQ11=sQuery(id+"F0.wireOp",EDGE,"E24.filletArc");Q0=makeQuery(id+"F2.boolean.opBoolean","SPLIT",FACE,{"disambiguationData":[TD([makeQuery(id+"F1.opExtrude","SWEPT_FACE",FACE,{"disambiguationData":[OSD([subQ5])]})])],"derivedFrom":makeQuery(id+"F1.opExtrude","CAP_FACE",FACE,{"disambiguationData":[OSD([subQ5,subQ7,subQ8,subQ9,subQ4,subQ3,subQ2,subQ1,subQ6,subQ0,subQ10,subQ11])],"isStart":true})});}
            var sketch = newSketch(context, id + "F16", { "sketchPlane" : qUnion([Q0])});
            skLineSegment(sketch, "E79", {"start": v(-80, 0) * mm, "end": v(80, 0) * mm});
            skLineSegment(sketch, "E80", {"start": v(-32.95, 90) * mm, "end": v(-14.95, 108) * mm});
            skLineSegment(sketch, "E81", {"start": v(-14.95, 108) * mm, "end": v(-14.95, 120) * mm});
            skLineSegment(sketch, "E82", {"start": v(15.04, 120.55) * mm, "end": v(15.04, 108) * mm});
            skLineSegment(sketch, "E83", {"start": v(15.04, 108) * mm, "end": v(33.04, 90) * mm});
            skLineSegment(sketch, "E84", {"start": v(0, 90) * mm, "end": v(0, 120) * mm});
            skCircle(sketch, "E85", {"center": v(0, 120) * mm, "radius": 6 * mm});
            skArc(sketch, "E86", {"start": v(15.04, 120.55) * mm, "mid": v(-0.23, 135.54) * mm, "end": v(-14.95, 120) * mm});
            skLineSegment(sketch, "E87.MirrorCS", {"start": v(15.04, -108) * mm, "end": v(33.04, -90) * mm});
            skLineSegment(sketch, "E88.MirrorCS", {"start": v(-32.95, -90) * mm, "end": v(-14.95, -108) * mm});
            skLineSegment(sketch, "E89.MirrorCS", {"start": v(-14.95, -108) * mm, "end": v(-14.95, -120) * mm});
            skLineSegment(sketch, "E90.MirrorCS", {"start": v(15.04, -120.55) * mm, "end": v(15.04, -108) * mm});
            skCircle(sketch, "E91.MirrorC", {"center": v(0, -120) * mm, "radius": 6 * mm});
            skLineSegment(sketch, "E92.MirrorCS", {"start": v(0, -90) * mm, "end": v(0, -120) * mm});
            skArc(sketch, "E93.MirrorCS", {"start": v(15.04, -120.55) * mm, "mid": v(-0.23, -135.54) * mm, "end": v(-14.95, -120) * mm});
            skSolve(sketch);
        }
        {
            var Q0;
            Q0=makeQuery(id+"F16.imprint","IMPRINT",FACE,{"disambiguationData":[TD([[makeQuery(id+"F16.imprint","IMPRINT",EDGE,{"derivedFrom":makeQuery(id+"F1.opExtrude","CAP_EDGE",EDGE,{"disambiguationData":[OSD([sQuery(id+"F0.wireOp",EDGE,"E4")])],"isStart":true})}),-1.0]])]});
            var Q1;
            Q1=makeQuery(id+"F16.imprint","IMPRINT",FACE,{"disambiguationData":[TD([[makeQuery(id+"F16.imprint","IMPRINT",EDGE,{"derivedFrom":makeQuery(id+"F1.opExtrude","CAP_EDGE",EDGE,{"disambiguationData":[OSD([sQuery(id+"F0.wireOp",EDGE,"E6")])],"isStart":true})}),-1.0]])]});
            var Q2;
            {var subQ0=sQuery(id+"F16.wireOp",EDGE,"E87.MirrorCS");Q2=makeQuery(id+"F16.imprint","IMPRINT",FACE,{"disambiguationData":[TD([[makeQuery(id+"F16.imprint","IMPRINT",EDGE,{"derivedFrom":subQ0}),1.0]])]});}
            var Q3;
            {var subQ0=sQuery(id+"F16.wireOp",EDGE,"E80");Q3=makeQuery(id+"F16.imprint","IMPRINT",FACE,{"disambiguationData":[TD([[makeQuery(id+"F16.imprint","IMPRINT",EDGE,{"derivedFrom":subQ0}),-1.0]])]});}
            var Q4;
            Q4=makeQuery(id+"F2.opExtrude","CAP_FACE",FACE,{"disambiguationData":[OSD([sQuery(id+"F0.wireOp",EDGE,"E12"),sQuery(id+"F0.wireOp",EDGE,"E13"),sQuery(id+"F0.wireOp",EDGE,"E14"),sQuery(id+"F0.wireOp",EDGE,"E15"),sQuery(id+"F0.wireOp",EDGE,"E17.filletArc"),sQuery(id+"F0.wireOp",EDGE,"E18.filletArc"),sQuery(id+"F0.wireOp",EDGE,"E19.filletArc"),sQuery(id+"F0.wireOp",EDGE,"E20.filletArc"),sQuery(id+"F0.wireOp",EDGE,"E25.0"),sQuery(id+"F0.wireOp",EDGE,"E25.1"),sQuery(id+"F0.wireOp",EDGE,"E25.2"),sQuery(id+"F0.wireOp",EDGE,"E25.3"),sQuery(id+"F0.wireOp",EDGE,"E25.4"),sQuery(id+"F0.wireOp",EDGE,"E25.5"),sQuery(id+"F0.wireOp",EDGE,"E25.6"),sQuery(id+"F0.wireOp",EDGE,"E25.7")])],"isStart":false});
            extrude(context, id + "F17", {"entities" : qUnion([Q0, Q1, Q2, Q3]), "endBound" : BoundingType.UP_TO_SURFACE, "endBoundEntityFace" : qUnion([Q4]), "depth" : 25 * mm});
        }
    });
